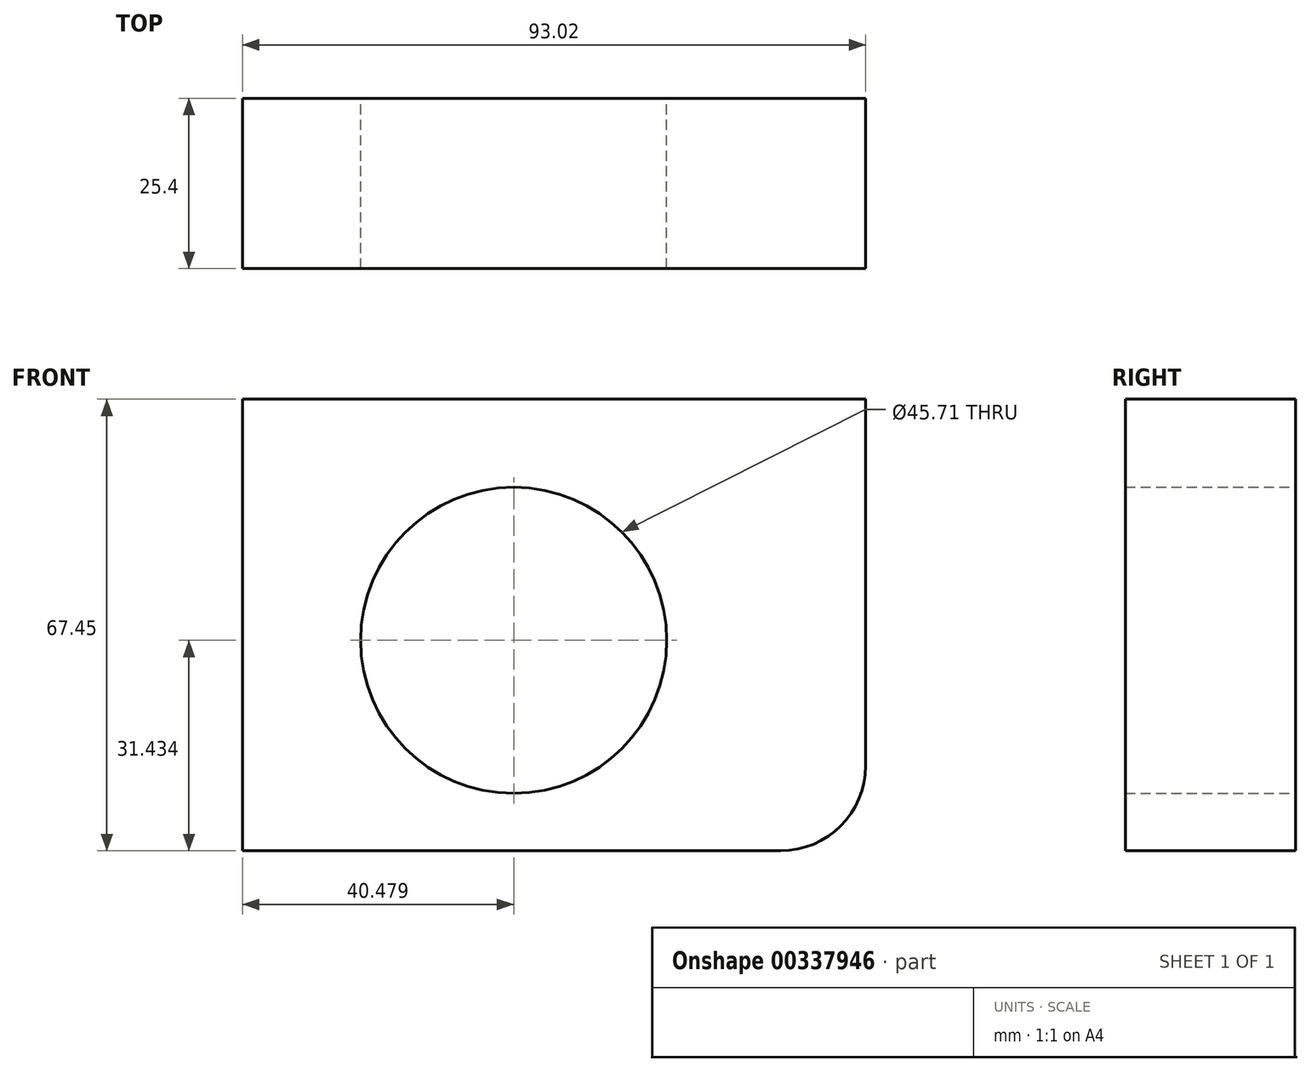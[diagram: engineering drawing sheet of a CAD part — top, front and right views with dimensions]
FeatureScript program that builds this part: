
annotation { "Feature Type Name" : "Feature", "Feature Type Description" : "" }
export const myFeature = defineFeature(function(context is Context, id is Id, definition is map)
    precondition{}
    {
        {
            var Q0;
            Q0=qCreatedBy(makeId("Front.planeOp"),FACE);
            var sketch = newSketch(context, id + "F0", { "sketchPlane" : qUnion([Q0])});
            skLineSegment(sketch, "E0.bottom", {"start": v(0, 0) * mm, "end": v(93.02, 0) * mm});
            skLineSegment(sketch, "E0.top", {"start": v(0, -67.45) * mm, "end": v(93.02, -67.45) * mm});
            skLineSegment(sketch, "E0.left", {"start": v(0, 0) * mm, "end": v(0, -67.45) * mm});
            skLineSegment(sketch, "E0.right", {"start": v(93.02, 0) * mm, "end": v(93.02, -67.45) * mm});
            skSolve(sketch);
        }
        {
            var Q0;
            Q0 = qSketchRegion(id + "F0", true);
            var sketch = newSketch(context, id + "F1", { "sketchPlane" : qUnion([Q0])});
            skSolve(sketch);
        }
        {
            var Q0;
            Q0=makeQuery(id+"F0.imprint","IMPRINT",FACE,{"disambiguationData":[TD([[makeQuery(id+"F0.imprint","IMPRINT",EDGE,{"derivedFrom":sQuery(id+"F0.wireOp",EDGE,"E0.bottom")}),-1.0]])]});
            extrude(context, id + "F2", {"entities" : qUnion([Q0]), "depth" : 25.4 * mm});
        }
        {
            var Q0;
            Q0=makeQuery(id+"F2.opExtrude","SWEPT_EDGE",EDGE,{"disambiguationData":[OSD([sQuery(id+"F0.wireOp",EDGE,"E0.top"),sQuery(id+"F0.wireOp",EDGE,"E0.right")])]});
            fillet(context, id + "F3", {"entities" : qUnion([Q0]), "radius" : 12.7 * mm, "tangentPropagation" : true, "allowEdgeOverflow" : false});
        }
        {
            var Q0;
            Q0=makeQuery(id+"F1.imprint","IMPRINT",FACE,{"disambiguationData":[TD([[makeQuery(id+"F1.imprint","IMPRINT",EDGE,{"derivedFrom":makeQuery(id+"F0.imprint","IMPRINT",EDGE,{"derivedFrom":sQuery(id+"F0.wireOp",EDGE,"E0.bottom")})}),-1.0]])]});
            var sketch = newSketch(context, id + "F4", { "sketchPlane" : qUnion([Q0])});
            skCircle(sketch, "E1", {"center": v(40.48, -36.02) * mm, "radius": 22.86 * mm});
            skSolve(sketch);
        }
        {
            var Q0;
            Q0=makeQuery(id+"F4.imprint","IMPRINT",FACE,{"disambiguationData":[TD([[makeQuery(id+"F4.imprint","IMPRINT",EDGE,{"derivedFrom":sQuery(id+"F4.wireOp",EDGE,"E1")}),1.0]])]});
            extrude(context, id + "F5", {"entities" : qUnion([Q0]), "operationType" : NewBodyOperationType.REMOVE, "depth" : 25.4 * mm});
        }
    });
